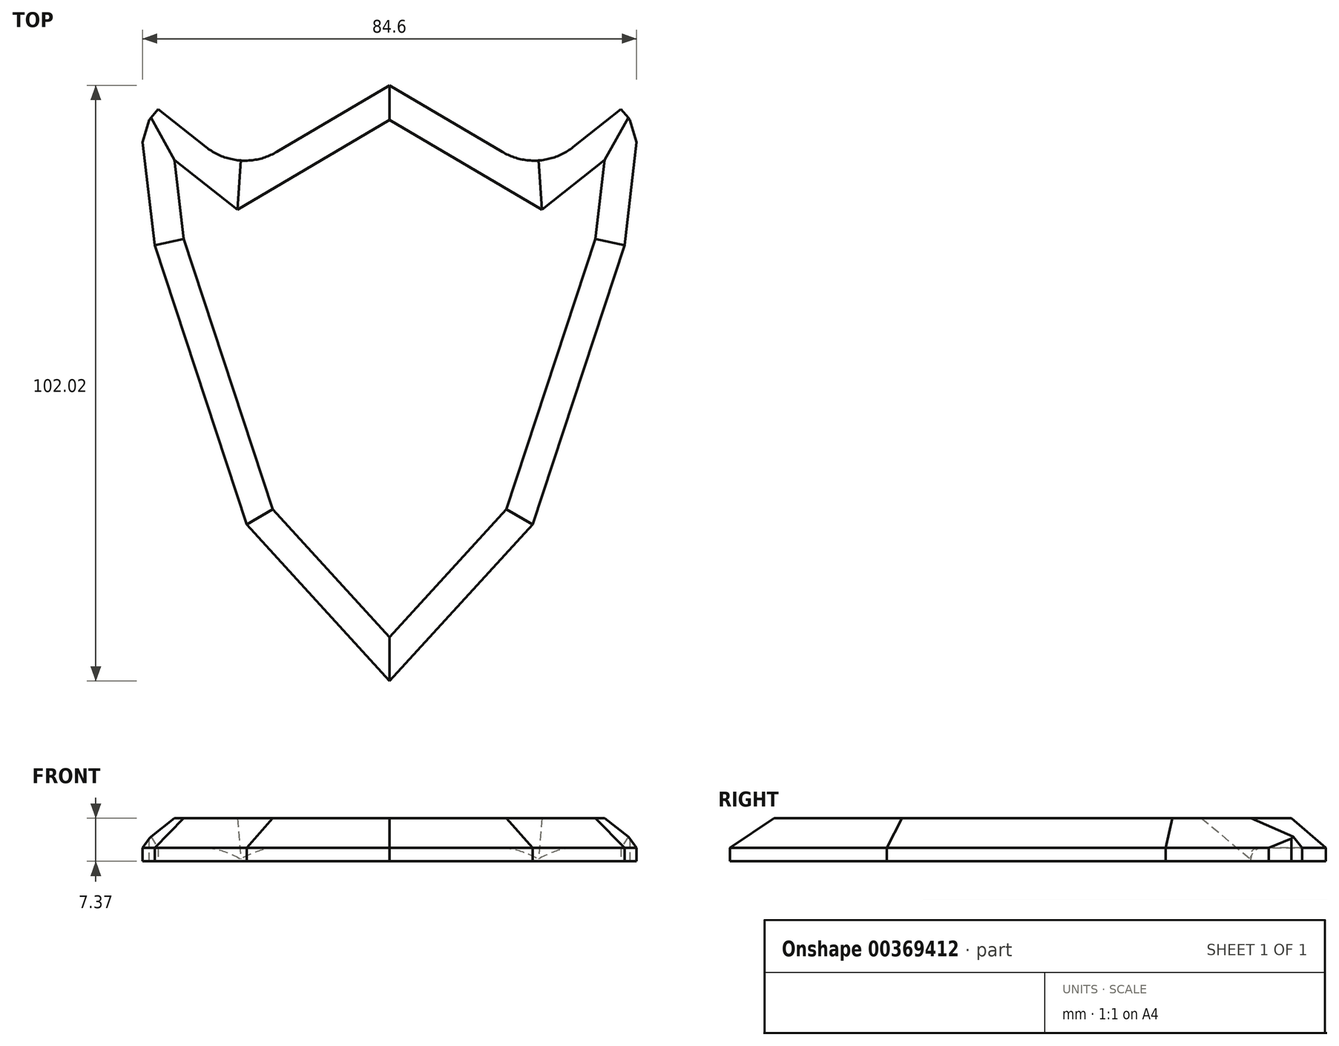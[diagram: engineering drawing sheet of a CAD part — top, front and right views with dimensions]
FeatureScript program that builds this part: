
annotation { "Feature Type Name" : "Feature", "Feature Type Description" : "" }
export const myFeature = defineFeature(function(context is Context, id is Id, definition is map)
    precondition{}
    {
        {
            var Q0;
            Q0=qCreatedBy(makeId("Top.planeOp"),FACE);
            var sketch = newSketch(context, id + "F0", { "sketchPlane" : qUnion([Q0])});
            skLineSegment(sketch, "E0", {"start": v(-25.65, 45.03) * mm, "end": v(0, 60.19) * mm});
            skLineSegment(sketch, "E1", {"start": v(-25.65, 45.03) * mm, "end": v(-39.64, 56.1) * mm});
            skLineSegment(sketch, "E2", {"start": v(-39.64, 56.1) * mm, "end": v(-42.56, 52.61) * mm});
            skLineSegment(sketch, "E3", {"start": v(-42.56, 52.61) * mm, "end": v(-40.22, 32.8) * mm});
            skLineSegment(sketch, "E4", {"start": v(-40.22, 32.8) * mm, "end": v(-24.48, -15.01) * mm});
            skLineSegment(sketch, "E5", {"start": v(-24.48, -15.01) * mm, "end": v(0, -41.83) * mm});
            skLineSegment(sketch, "E6.MirrorCS", {"start": v(39.64, 56.1) * mm, "end": v(42.56, 52.61) * mm});
            skLineSegment(sketch, "E7.MirrorCS", {"start": v(25.65, 45.03) * mm, "end": v(39.64, 56.1) * mm});
            skLineSegment(sketch, "E8.MirrorCS", {"start": v(40.22, 32.8) * mm, "end": v(24.48, -15.01) * mm});
            skLineSegment(sketch, "E9.MirrorCS", {"start": v(24.48, -15.01) * mm, "end": v(0, -41.83) * mm});
            skLineSegment(sketch, "E10.MirrorCS", {"start": v(42.56, 52.61) * mm, "end": v(40.22, 32.8) * mm});
            skLineSegment(sketch, "E11.MirrorCS", {"start": v(25.65, 45.03) * mm, "end": v(0, 60.19) * mm});
            skSolve(sketch);
        }
        {
            var Q0;
            Q0=makeQuery(id+"F0.imprint","IMPRINT",FACE,{"disambiguationData":[TD([[makeQuery(id+"F0.imprint","IMPRINT",EDGE,{"derivedFrom":sQuery(id+"F0.wireOp",EDGE,"E0")}),-1.0]])]});
            extrude(context, id + "F1", {"entities" : qUnion([Q0]), "depth" : 7.37 * mm});
        }
        {
            var Q0;
            Q0=makeQuery(id+"F1.opExtrude","CAP_EDGE",EDGE,{"disambiguationData":[OSD([sQuery(id+"F0.wireOp",EDGE,"E2")])],"isStart":false});
            var Q1;
            Q1=makeQuery(id+"F1.opExtrude","CAP_EDGE",EDGE,{"disambiguationData":[OSD([sQuery(id+"F0.wireOp",EDGE,"E6.MirrorCS")])],"isStart":false});
            var Q2;
            Q2=makeQuery(id+"F1.opExtrude","CAP_EDGE",EDGE,{"disambiguationData":[OSD([sQuery(id+"F0.wireOp",EDGE,"E7.MirrorCS")])],"isStart":false});
            var Q3;
            Q3=makeQuery(id+"F1.opExtrude","CAP_EDGE",EDGE,{"disambiguationData":[OSD([sQuery(id+"F0.wireOp",EDGE,"E11.MirrorCS")])],"isStart":false});
            var Q4;
            Q4=makeQuery(id+"F1.opExtrude","CAP_EDGE",EDGE,{"disambiguationData":[OSD([sQuery(id+"F0.wireOp",EDGE,"E0")])],"isStart":false});
            var Q5;
            Q5=makeQuery(id+"F1.opExtrude","CAP_EDGE",EDGE,{"disambiguationData":[OSD([sQuery(id+"F0.wireOp",EDGE,"E1")])],"isStart":false});
            var Q6;
            Q6=makeQuery(id+"F1.opExtrude","CAP_EDGE",EDGE,{"disambiguationData":[OSD([sQuery(id+"F0.wireOp",EDGE,"E3")])],"isStart":false});
            var Q7;
            Q7=makeQuery(id+"F1.opExtrude","CAP_EDGE",EDGE,{"disambiguationData":[OSD([sQuery(id+"F0.wireOp",EDGE,"E4")])],"isStart":false});
            var Q8;
            Q8=makeQuery(id+"F1.opExtrude","CAP_EDGE",EDGE,{"disambiguationData":[OSD([sQuery(id+"F0.wireOp",EDGE,"E5")])],"isStart":false});
            var Q9;
            Q9=makeQuery(id+"F1.opExtrude","CAP_EDGE",EDGE,{"disambiguationData":[OSD([sQuery(id+"F0.wireOp",EDGE,"E9.MirrorCS")])],"isStart":false});
            var Q10;
            Q10=makeQuery(id+"F1.opExtrude","CAP_EDGE",EDGE,{"disambiguationData":[OSD([sQuery(id+"F0.wireOp",EDGE,"E8.MirrorCS")])],"isStart":false});
            var Q11;
            Q11=makeQuery(id+"F1.opExtrude","CAP_EDGE",EDGE,{"disambiguationData":[OSD([sQuery(id+"F0.wireOp",EDGE,"E10.MirrorCS")])],"isStart":false});
            chamfer(context, id + "F2", {"entities" : qUnion([Q0, Q1, Q2, Q3, Q4, Q5, Q6, Q7, Q8, Q9, Q10, Q11]), "width" : 5.08 * mm, "tangentPropagation" : true});
        }
        {
            var Q0;
            Q0=makeQuery(id+"F1.opExtrude","SWEPT_EDGE",EDGE,{"disambiguationData":[OSD([sQuery(id+"F0.wireOp",EDGE,"E0"),sQuery(id+"F0.wireOp",EDGE,"E1")])]});
            var Q1;
            Q1=makeQuery(id+"F1.opExtrude","SWEPT_EDGE",EDGE,{"disambiguationData":[OSD([sQuery(id+"F0.wireOp",EDGE,"E7.MirrorCS"),sQuery(id+"F0.wireOp",EDGE,"E11.MirrorCS")])]});
            fillet(context, id + "F3", {"entities" : qUnion([Q0, Q1]), "radius" : 10.73 * mm, "tangentPropagation" : true, "allowEdgeOverflow" : false});
        }
        {
            var Q0;
            Q0=makeQuery(id+"F1.opExtrude","SWEPT_EDGE",EDGE,{"disambiguationData":[OSD([sQuery(id+"F0.wireOp",EDGE,"E2"),sQuery(id+"F0.wireOp",EDGE,"E3")])]});
            var Q1;
            Q1=makeQuery(id+"F1.opExtrude","SWEPT_EDGE",EDGE,{"disambiguationData":[OSD([sQuery(id+"F0.wireOp",EDGE,"E6.MirrorCS"),sQuery(id+"F0.wireOp",EDGE,"E10.MirrorCS")])]});
            chamfer(context, id + "F4", {"entities" : qUnion([Q0, Q1]), "width" : 5.08 * mm, "tangentPropagation" : true});
        }
    });
